# Revit family: Toilet-Floor_Mount-KOHLER-Reach_Up-K-23188K
name_source: partatom
category: Plumbing Fixtures
units: mm (PartAtom-declared; Revit-internal decimal feet)

## family parameters
Cut with Voids When Loaded = No
Host = Face
Maintain Annotation Orientation = No
OmniClass Number = 23.31.19.00
Part Type = Normal
Room Calculation Point = No
Round Connector Dimension = Use Diameter
Shared = No

## types (1)
- 0-White
    ADA Compliant = No
    Apparent Load = 2200 VA
    Assembly Code = D2010100
    Bowl Height = 15 9/16"
    CW Connection = Yes
    Cold Water Inlet 1 = Cold Water Inlet 1
    Cold Water Inlet 2 = Cold Water Inlet 2
    Date Modified = 07/03/2025
    Default Elevation = 0"
    Description = Family Care skirted I PC 305 mm without seat
    Electrical Connector = Yes
    Electrical Note = One Dedicated circuit Required
    Finish = Kohler-Vitreous_China-0-White
    Flow Rate = 0 GPM
    Flush Rate- GPF = 1.28 GPF
    Flush Rate- LPF = 4.8 LPF
    HW Connection = No
    Height = 29 9/16"
    Hot Water Inlet = Hot Water Inlet
    Length = 27 9/16"
    Manufacturer = Kohler Co.
    Master Format 2014 = 22 42 13.13
    Master Format 2014 Name = Residential Water Closets
    Material = Vitreous China
    Model = K-23188K-NS-0
    Pressure = 0.00 psi
    Product Name = Reach Up
    Rough-In = 12"
    Seat Included = No
    Type = 1
    URL = https://www.kohlerasiapacific.com
    Vent Connection = No
    Voltage = 220 V
    Waste Connection = Yes
    Waste Water Outlet = Waste Water Outlet
    WaterSense Certified = No
    Width = 14 7/8"

## geometry (parser evidence)
native form markers: Sweep x10
no freeform markers — native parametric forms only
